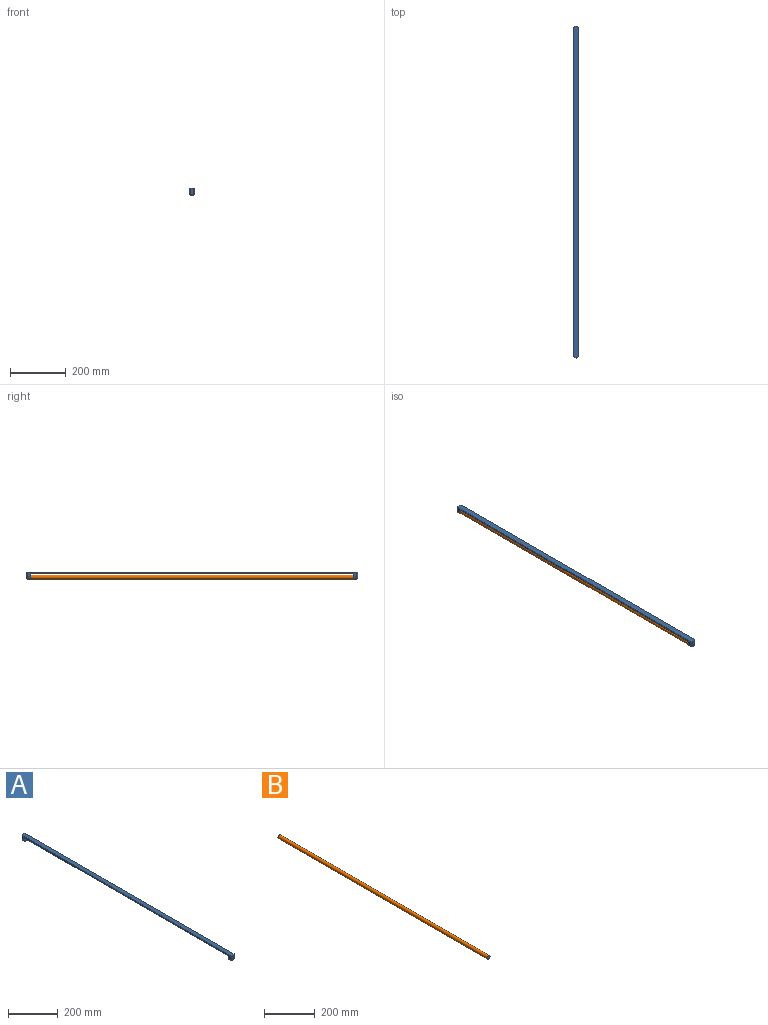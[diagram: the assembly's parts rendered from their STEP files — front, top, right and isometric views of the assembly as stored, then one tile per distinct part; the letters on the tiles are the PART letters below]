
ASSEMBLY  parts=2 mates=1
PART A: 16 faces, bbox 20x1193x27 mm
  f0: plane 1193x20mm, normal (0,0,1), area 23810mm2, adj f1,f3,f4,f6,f8,f11,f12,f14
  f1: plane 1183x17mm, normal (-1,0,0), area 7318mm2, adj f0,f2,f5,f8,f9,f10,f14,f15
  f2: cylinder r=10mm len=20mm, axis (0,1,0), area 314.2mm2, adj f1,f3,f5,f7
  f3: plane 1183x17mm, normal (1,0,0), area 7318mm2, adj f0,f2,f5,f6,f9,f10,f12,f15
  f4: plane 22x10mm, normal (0,-1,0), area 209.3mm2, adj f0,f6,f7,f8
  f5: plane 21x20mm, normal (0,1,0), area 377.1mm2, adj f1,f2,f3,f15
  f6: plane 17x5mm, normal (0.71,-0.71,0), area 120.2mm2, adj f0,f3,f4,f7
  f7: cone r=5mm half-angle=45deg, axis (0,1,0), area 166.6mm2, adj f2,f4,f6,f8
  f8: plane 17x5mm, normal (-0.71,-0.71,0), area 120.2mm2, adj f0,f1,f4,f7
  f9: plane 21x20mm, normal (0,-1,0), area 377.1mm2, adj f1,f3,f10,f15
  f10: cylinder r=10mm len=20mm, axis (0,-1,0), area 314.2mm2, adj f1,f3,f9,f13
  f11: plane 22x10mm, normal (0,1,0), area 209.3mm2, adj f0,f12,f13,f14
  f12: plane 17x5mm, normal (0.71,0.71,0), area 120.2mm2, adj f0,f3,f11,f13
  f13: cone r=5mm half-angle=45deg, axis (0,-1,0), area 166.6mm2, adj f10,f11,f12,f14
  f14: plane 17x5mm, normal (-0.71,0.71,0), area 120.2mm2, adj f0,f1,f11,f13
  f15: plane 1163x20mm, normal (0,0,-1), area 23260mm2, adj f1,f3,f5,f9
PART B: 3 faces, bbox 15.9x1163x15.9 mm
  f0: cylinder r=7.94mm len=1163mm, axis (0,1,0), area 58002mm2, adj f1,f2
  f1: plane 15.88x15.88mm, normal (0,-1,0), area 197.9mm2, adj f0
  f2: plane 15.88x15.88mm, normal (0,1,0), area 197.9mm2, adj f0
PLACE A t=(-153.02,14.83,153.26)mm
PLACE B t=(-153.02,14.83,151.26)mm
MATE fastened B.f0 <-> A.f2  axis (0,1,0) through (-153.02,-566.67,151.26)mm
